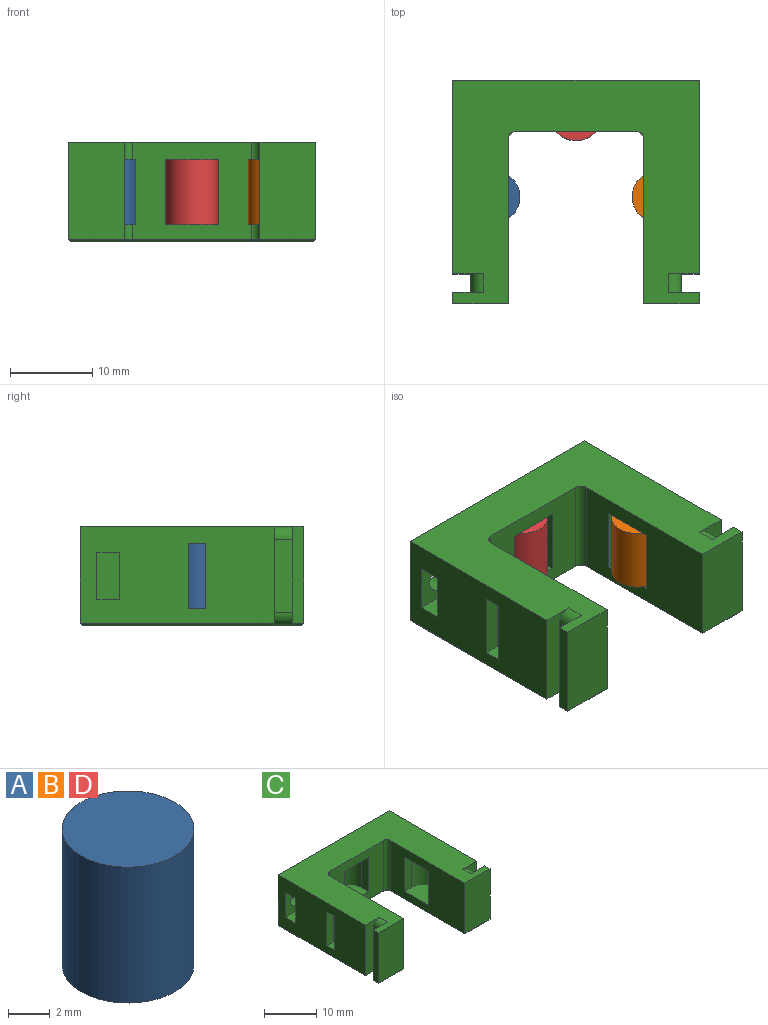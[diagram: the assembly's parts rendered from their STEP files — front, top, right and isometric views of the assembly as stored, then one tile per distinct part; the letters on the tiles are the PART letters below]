
ASSEMBLY  parts=4 mates=3
PART A: 3 faces, bbox 6.4x6.4x8 mm
  f0: cylinder r=3.17mm len=8mm, axis (0,0,-1), area 159.6mm2, adj f1,f2
  f1: plane 6.35x6.35mm, normal (0,0,1), area 31.7mm2, adj f0
  f2: plane 6.35x6.35mm, normal (0,0,-1), area 31.7mm2, adj f0
PART B: same geometry as A
PART C: 80 faces, bbox 30x27.2x12 mm
  f0: plane 20x11.75mm, normal (1,0,0), area 182.6mm2, adj f4,f16,f36,f37,f39,f40,f58,f67
  f1: plane 9x2.2mm, normal (-1,0,0), area 19.8mm2, adj f2,f15,f61,f63
  f2: plane 11.75x3.7mm, normal (0,1,0), area 26.6mm2, adj f1,f3,f16,f61,f63,f64
  f3: plane 11.75x1.4mm, normal (-1,0,0), area 16.5mm2, adj f2,f4,f16,f65
  f4: plane 11.75x6.75mm, normal (0,-1,0), area 79.3mm2, adj f0,f3,f16,f66
  f5: plane 14.5x11.75mm, normal (0,-1,0), area 118mm2, adj f16,f46,f47,f48,f49,f58,f59,f69
  f6: plane 20x11.75mm, normal (-1,0,0), area 182.6mm2, adj f7,f16,f54,f55,f56,f57,f59,f71
  f7: plane 11.75x6.75mm, normal (0,-1,0), area 79.3mm2, adj f6,f8,f16,f72
  f8: plane 11.75x1.4mm, normal (1,0,0), area 16.4mm2, adj f7,f9,f16,f73
  f9: plane 11.75x3.7mm, normal (0,1,0), area 26.6mm2, adj f8,f10,f16,f60,f62,f74
  f10: plane 9x2.2mm, normal (1,0,0), area 19.8mm2, adj f9,f11,f60,f62
  f11: plane 11.75x3.7mm, normal (0,-1,0), area 26.6mm2, adj f10,f12,f16,f60,f62,f79
  f12: plane 23.59x11.75mm, normal (1,0,0), area 245mm2, adj f11,f13,f16,f23,f25,f26,f27,f51
  f13: plane 30x11.75mm, normal (0,1,0), area 320.4mm2, adj f12,f14,f16,f28,f33,f43,f44,f48
  f14: plane 23.59x11.75mm, normal (-1,0,0), area 245mm2, adj f13,f15,f16,f18,f20,f21,f22,f34
  f15: plane 11.75x3.7mm, normal (0,-1,0), area 26.6mm2, adj f1,f14,f16,f61,f63,f75
  f16: plane 30x27.19mm, normal (0,0,1), area 453.4mm2, adj f0,f2,f3,f4,f5,f6,f7,f8
  f17: plane 29.5x26.69mm, normal (0,0,-1), area 412.4mm2, adj f60,f61,f64,f65,f66,f67,f68,f69
  f18: plane 6x5.8mm, normal (0,1,0), area 26.8mm2, adj f14,f19,f21,f22,f29
  f19: plane 5.8x2.8mm, normal (-1,0,0), area 16.2mm2, adj f18,f20,f21,f22
  f20: plane 6x5.8mm, normal (0,-1,0), area 26.8mm2, adj f14,f19,f21,f22,f28
  f21: plane 6x2.8mm, normal (0,0,-1), area 16.8mm2, adj f14,f18,f19,f20
  f22: plane 6x2.8mm, normal (0,0,1), area 16.8mm2, adj f14,f18,f19,f20
  f23: plane 6x5.8mm, normal (0,-1,0), area 26.8mm2, adj f12,f24,f26,f27,f33
  f24: plane 5.8x2.8mm, normal (1,0,0), area 16.2mm2, adj f23,f25,f26,f27
  f25: plane 6x5.8mm, normal (0,1,0), area 26.8mm2, adj f12,f24,f26,f27,f31
  f26: plane 6x2.8mm, normal (0,0,-1), area 16.8mm2, adj f12,f23,f24,f25
  f27: plane 6x2.8mm, normal (0,0,1), area 16.8mm2, adj f12,f23,f24,f25
  f28: cylinder r=1.6mm len=3.2mm, axis (0,1,0), area 20.1mm2, adj f13,f20
  f29: cylinder r=1.6mm len=3.2mm, axis (0,1,0), area 15.1mm2, adj f18,f30
  f30: plane 3.2x3.2mm, normal (0,1,0), area 8mm2, adj f29
  f31: cylinder r=1.6mm len=3.2mm, axis (0,1,0), area 15.1mm2, adj f25,f32
  f32: plane 3.2x3.2mm, normal (0,1,0), area 8mm2, adj f31
  f33: cylinder r=1.6mm len=3.2mm, axis (0,1,0), area 20.1mm2, adj f13,f23
  f34: plane 8x1.87mm, normal (0,1,0), area 14.9mm2, adj f14,f36,f37,f38
  f35: plane 8x1.87mm, normal (0,-1,0), area 14.9mm2, adj f14,f36,f37,f41
  f36: plane 6.75x6.55mm, normal (0,0,-1), area 31.9mm2, adj f0,f14,f34,f35,f38,f39,f40,f41
  f37: plane 6.75x6.55mm, normal (0,0,1), area 31.9mm2, adj f0,f14,f34,f35,f38,f39,f40,f41
  f38: cylinder r=3.28mm len=8mm, axis (0,0,-1), area 33mm2, adj f34,f36,f37,f39
  f39: plane 8x1.77mm, normal (0,1,0), area 14.1mm2, adj f0,f36,f37,f38
  f40: plane 8x1.77mm, normal (0,-1,0), area 14.1mm2, adj f0,f36,f37,f41
  f41: cylinder r=3.28mm len=8mm, axis (0,0,-1), area 33mm2, adj f35,f36,f37,f40
  f42: cylinder r=3.28mm len=8mm, axis (0,0,-1), area 33mm2, adj f43,f47,f48,f49
  f43: plane 8x1.06mm, normal (-1,0,0), area 8.5mm2, adj f13,f42,f48,f49
  f44: plane 8x1.06mm, normal (1,0,0), area 8.5mm2, adj f13,f45,f48,f49
  f45: cylinder r=3.28mm len=8mm, axis (0,0,-1), area 33mm2, adj f44,f46,f48,f49
  f46: plane 8x2.02mm, normal (1,0,0), area 16.1mm2, adj f5,f45,f48,f49
  f47: plane 8x2.02mm, normal (-1,0,0), area 16.1mm2, adj f5,f42,f48,f49
  f48: plane 6.55x6.19mm, normal (0,0,-1), area 32mm2, adj f5,f13,f42,f43,f44,f45,f46,f47
  f49: plane 6.55x6.19mm, normal (0,0,1), area 32mm2, adj f5,f13,f42,f43,f44,f45,f46,f47
  f50: cylinder r=3.28mm len=8mm, axis (0,0,-1), area 33mm2, adj f51,f55,f56,f57
  f51: plane 8x1.87mm, normal (0,1,0), area 14.9mm2, adj f12,f50,f56,f57
  f52: plane 8x1.87mm, normal (0,-1,0), area 14.9mm2, adj f12,f53,f56,f57
  f53: cylinder r=3.28mm len=8mm, axis (0,0,-1), area 33mm2, adj f52,f54,f56,f57
  f54: plane 8x1.77mm, normal (0,-1,0), area 14.1mm2, adj f6,f53,f56,f57
  f55: plane 8x1.77mm, normal (0,1,0), area 14.1mm2, adj f6,f50,f56,f57
  f56: plane 6.75x6.55mm, normal (0,0,-1), area 31.9mm2, adj f6,f12,f50,f51,f52,f53,f54,f55
  f57: plane 6.75x6.55mm, normal (0,0,1), area 31.9mm2, adj f6,f12,f50,f51,f52,f53,f54,f55
  f58: cylinder r=1mm len=11.75mm, axis (0,0,1), area 18.5mm2, adj f0,f5,f16,f68
  f59: cylinder r=1mm len=11.75mm, axis (0,0,-1), area 18.5mm2, adj f5,f6,f16,f70
  f60: cylinder r=1.5mm len=2.7mm, axis (0,1,0), area 5.5mm2, adj f9,f10,f11,f17,f74,f79
  f61: cylinder r=1.5mm len=2.7mm, axis (0,-1,0), area 5.5mm2, adj f1,f2,f15,f17,f64,f75
  f62: cylinder r=1.5mm len=2.2mm, axis (0,-1,0), area 5.2mm2, adj f9,f10,f11,f16
  f63: cylinder r=1.5mm len=2.2mm, axis (0,1,0), area 5.2mm2, adj f1,f2,f15,f16
  f64: plane 3.7x0.25mm, normal (0,0.71,-0.71), area 1.1mm2, adj f2,f17,f61,f65
  f65: plane 1.4x0.25mm, normal (-0.71,0,-0.71), area 0.4mm2, adj f3,f17,f64,f66
  f66: plane 6.75x0.25mm, normal (0,-0.71,-0.71), area 2.3mm2, adj f4,f17,f65,f67
  f67: plane 20x0.25mm, normal (0.71,0,-0.71), area 7mm2, adj f0,f17,f66,f68
  f68: cone r=1.25mm half-angle=45deg, axis (0,0,-1), area 0.6mm2, adj f17,f58,f67,f69
  f69: plane 14.5x0.25mm, normal (0,-0.71,-0.71), area 5.1mm2, adj f5,f17,f68,f70
  f70: cone r=1.25mm half-angle=45deg, axis (0,0,-1), area 0.6mm2, adj f17,f59,f69,f71
  f71: plane 20x0.25mm, normal (-0.71,0,-0.71), area 7mm2, adj f6,f17,f70,f72
  f72: plane 6.75x0.25mm, normal (0,-0.71,-0.71), area 2.3mm2, adj f7,f17,f71,f73
  f73: plane 1.4x0.25mm, normal (0.71,0,-0.71), area 0.4mm2, adj f8,f17,f72,f74
  f74: plane 3.7x0.25mm, normal (0,0.71,-0.71), area 1.1mm2, adj f9,f17,f60,f73
  f75: plane 3.7x0.25mm, normal (0,-0.71,-0.71), area 1.1mm2, adj f15,f17,f61,f76
  f76: plane 23.59x0.25mm, normal (-0.71,0,-0.71), area 8.3mm2, adj f14,f17,f75,f77
  f77: plane 30x0.25mm, normal (0,0.71,-0.71), area 10.5mm2, adj f13,f17,f76,f78
  f78: plane 23.59x0.25mm, normal (0.71,0,-0.71), area 8.3mm2, adj f12,f17,f77,f79
  f79: plane 3.7x0.25mm, normal (0,-0.71,-0.71), area 1.1mm2, adj f11,f17,f60,f78
PART D: same geometry as A
PLACE A t=(-10.24,0.03,0.27)mm
PLACE B t=(9.79,0.03,0.27)mm
PLACE C t=(-0.22,0.03,0.27)mm fixed
PLACE D t=(-0.22,10.04,0.27)mm
MATE fastened A.f0 <-> C.f41  axis (0,0,-1) through (-10.24,0.03,-3.73)mm
MATE fastened D.f0 <-> C.f42  axis (0,0,-1) through (-0.22,10.04,-3.73)mm
MATE fastened B.f0 <-> C.f50  axis (0,0,-1) through (9.79,0.03,-3.73)mm
